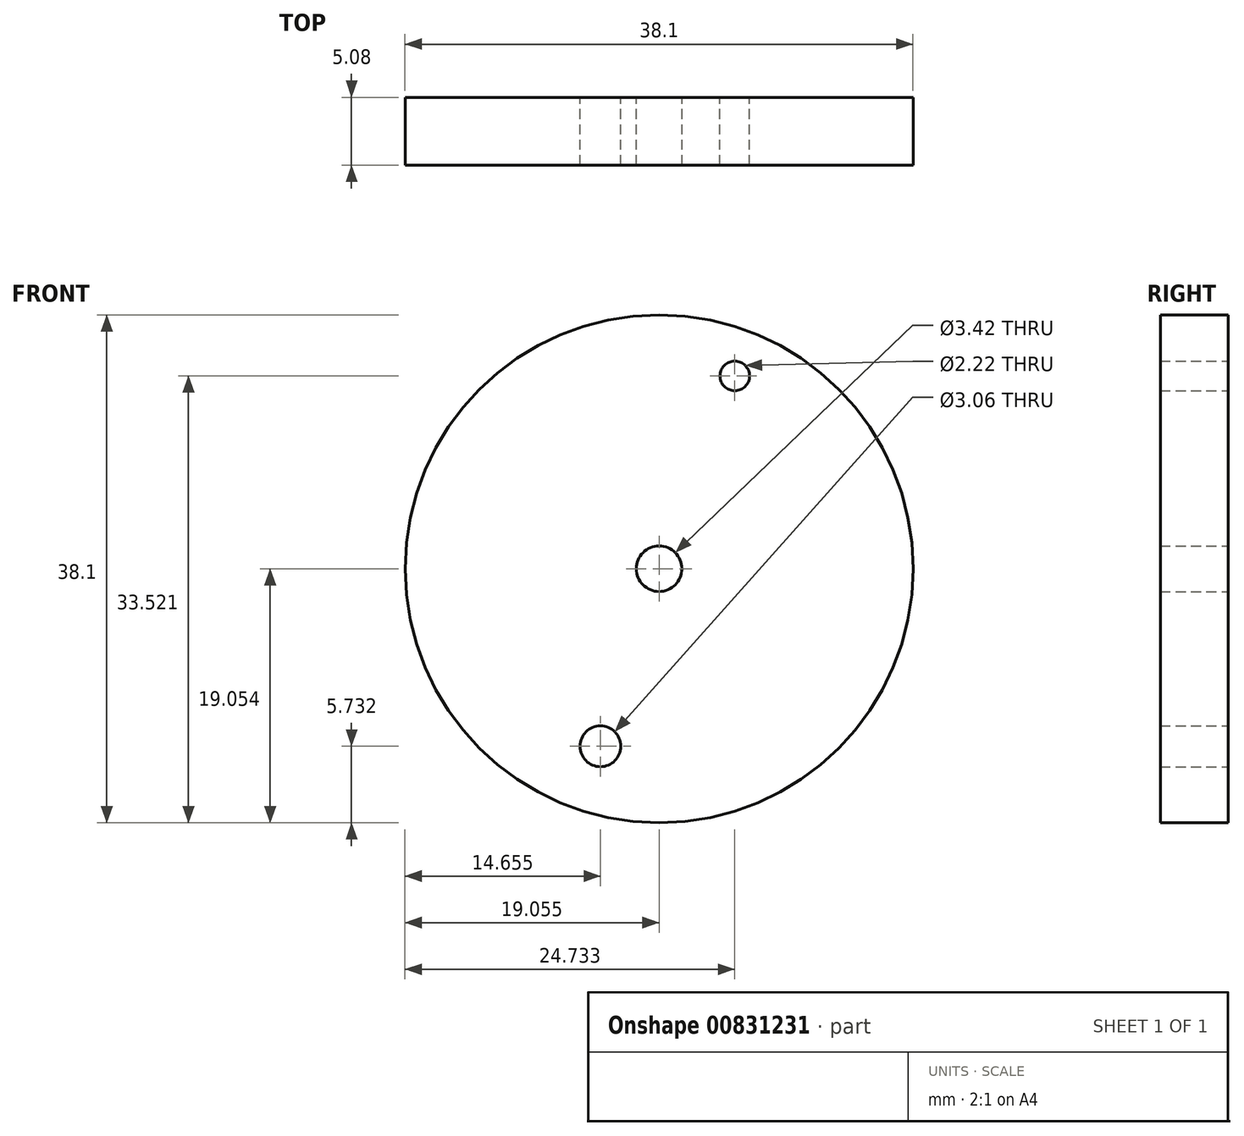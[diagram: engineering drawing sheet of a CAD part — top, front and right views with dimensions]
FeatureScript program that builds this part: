
annotation { "Feature Type Name" : "Feature", "Feature Type Description" : "" }
export const myFeature = defineFeature(function(context is Context, id is Id, definition is map)
    precondition{}
    {
        {
            var Q0;
            Q0=qCreatedBy(makeId("Front.planeOp"),FACE);
            var sketch = newSketch(context, id + "F0", { "sketchPlane" : qUnion([Q0])});
            skCircle(sketch, "E0", {"center": v(-56.26, 38.64) * mm, "radius": 19.05 * mm});
            skCircle(sketch, "E1", {"center": v(-56.26, 38.64) * mm, "radius": 1.71 * mm});
            skCircle(sketch, "E2", {"center": v(-50.58, 53.11) * mm, "radius": 1.11 * mm});
            skCircle(sketch, "E3", {"center": v(-60.66, 25.32) * mm, "radius": 1.53 * mm});
            skSolve(sketch);
        }
        {
            var Q0;
            Q0=makeQuery(id+"F0.imprint","IMPRINT",FACE,{"disambiguationData":[TD([[makeQuery(id+"F0.imprint","IMPRINT",EDGE,{"derivedFrom":sQuery(id+"F0.wireOp",EDGE,"E0")}),1.0]])]});
            extrude(context, id + "F1", {"entities" : qUnion([Q0]), "depth" : 5.08 * mm, "offsetDistance" : 25.4 * mm});
        }
    });
